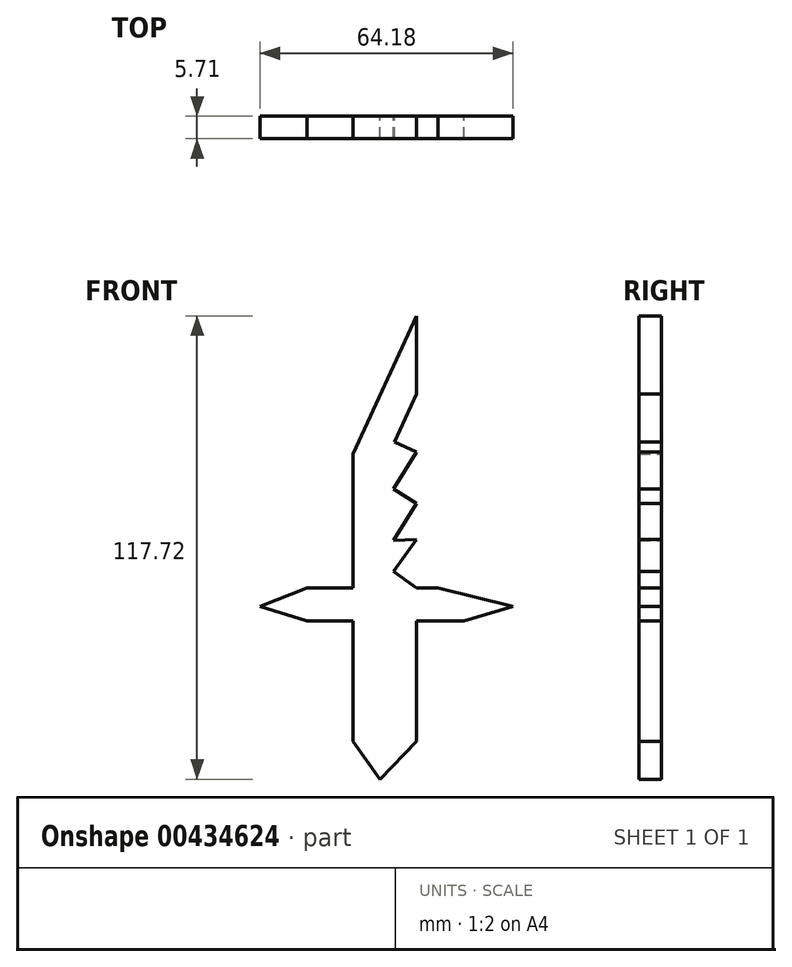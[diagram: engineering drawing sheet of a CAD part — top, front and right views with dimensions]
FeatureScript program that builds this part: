
annotation { "Feature Type Name" : "Feature", "Feature Type Description" : "" }
export const myFeature = defineFeature(function(context is Context, id is Id, definition is map)
    precondition{}
    {
        {
            var Q0;
            Q0=qCreatedBy(makeId("Front.planeOp"),FACE);
            var sketch = newSketch(context, id + "F0", { "sketchPlane" : qUnion([Q0])});
            skLineSegment(sketch, "E0", {"start": v(-9.9, 43.28) * mm, "end": v(-26, 8.2) * mm});
            skLineSegment(sketch, "E1", {"start": v(-9.9, 43.28) * mm, "end": v(-9.9, 23.38) * mm});
            skLineSegment(sketch, "E2", {"start": v(-26, 8.2) * mm, "end": v(-26, -25.84) * mm});
            skLineSegment(sketch, "E3", {"start": v(-9.9, 23.38) * mm, "end": v(-15.5, 11.2) * mm});
            skLineSegment(sketch, "E4", {"start": v(-15.5, 11.2) * mm, "end": v(-9.9, 8.72) * mm});
            skLineSegment(sketch, "E5", {"start": v(-9.9, 8.72) * mm, "end": v(-15.79, -0.69) * mm});
            skLineSegment(sketch, "E6", {"start": v(-15.79, -0.69) * mm, "end": v(-9.9, -4.37) * mm});
            skLineSegment(sketch, "E7", {"start": v(-9.9, -4.37) * mm, "end": v(-15.79, -13.77) * mm});
            skLineSegment(sketch, "E8", {"start": v(-15.79, -13.77) * mm, "end": v(-9.9, -13.49) * mm});
            skLineSegment(sketch, "E9", {"start": v(-9.9, -13.49) * mm, "end": v(-15.79, -21.6) * mm});
            skLineSegment(sketch, "E10", {"start": v(-15.79, -21.6) * mm, "end": v(-9.9, -25.87) * mm});
            skLineSegment(sketch, "E11", {"start": v(-37.76, -25.84) * mm, "end": v(-4.49, -25.84) * mm});
            skLineSegment(sketch, "E12", {"start": v(-37.76, -25.84) * mm, "end": v(-49.63, -30.49) * mm});
            skLineSegment(sketch, "E13", {"start": v(-49.63, -30.49) * mm, "end": v(-37.76, -34.2) * mm});
            skLineSegment(sketch, "E14", {"start": v(-37.76, -34.2) * mm, "end": v(2.17, -34.2) * mm});
            skLineSegment(sketch, "E15", {"start": v(2.17, -34.2) * mm, "end": v(14.55, -30.49) * mm});
            skLineSegment(sketch, "E16", {"start": v(14.55, -30.49) * mm, "end": v(-4.49, -25.84) * mm});
            skLineSegment(sketch, "E17", {"start": v(-26, -34.2) * mm, "end": v(-26, -64.84) * mm});
            skLineSegment(sketch, "E18", {"start": v(-26, -64.84) * mm, "end": v(-19.2, -74.44) * mm});
            skLineSegment(sketch, "E19", {"start": v(-9.9, -34.2) * mm, "end": v(-9.9, -64.84) * mm});
            skLineSegment(sketch, "E20", {"start": v(-9.9, -64.84) * mm, "end": v(-19.2, -74.44) * mm});
            skLineSegment(sketch, "E21.trimOffspring", {"start": v(-9.9, -25.84) * mm, "end": v(-9.9, -25.87) * mm});
            skSolve(sketch);
        }
        {
            var Q0;
            Q0 = qSketchRegion(id + "F0", true);
            extrude(context, id + "F1", {"entities" : qUnion([Q0]), "depth" : 5.7 * mm});
        }
    });
